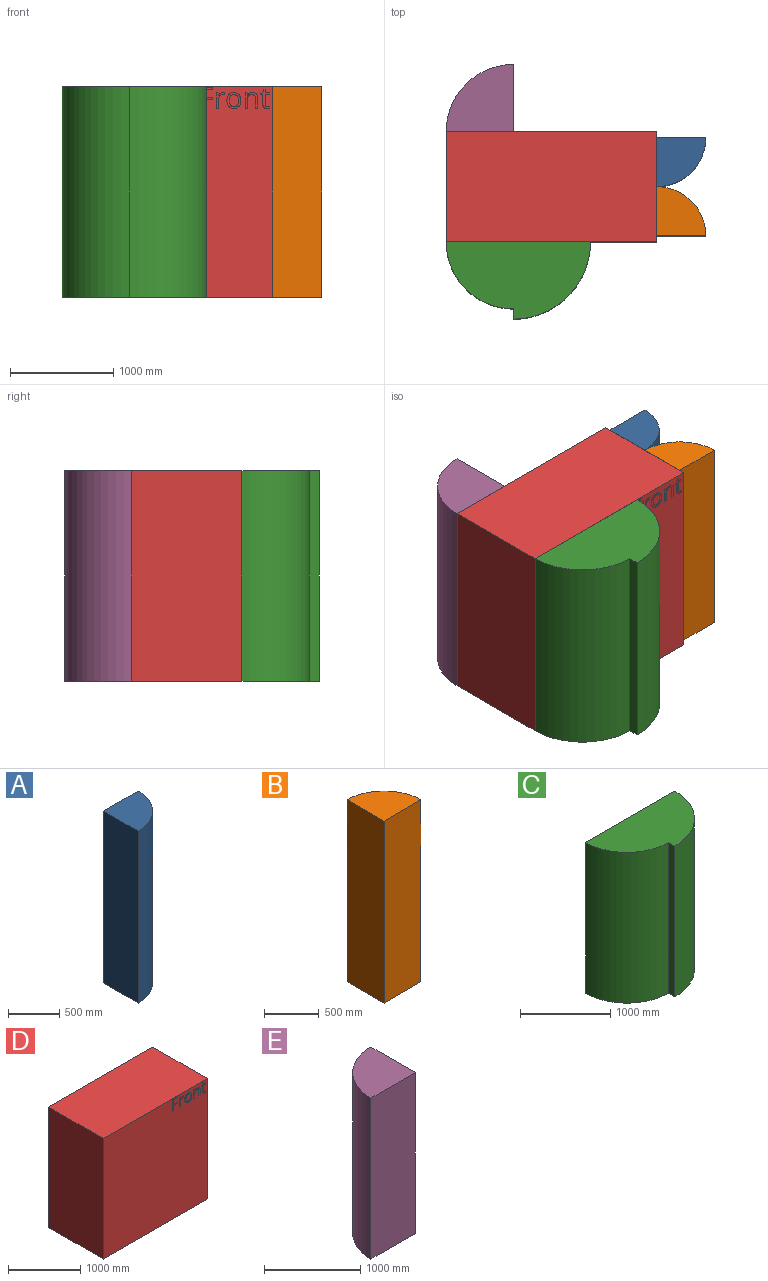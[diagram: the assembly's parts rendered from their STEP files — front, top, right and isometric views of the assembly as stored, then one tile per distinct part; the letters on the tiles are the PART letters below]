
ASSEMBLY  parts=5 mates=8
PART A: 5 faces, bbox 478x478x2045 mm
  f0: plane 2045x478mm, normal (-1,0,0), area 977510mm2, adj f1,f2,f3,f4
  f1: cylinder r=478mm len=2045mm, axis (0,0,-1), area 1535469.1mm2, adj f0,f2,f3,f4
  f2: plane 2045x478mm, normal (0,1,0), area 977510mm2, adj f0,f1,f3,f4
  f3: plane 478x478mm, normal (0,0,1), area 179450.9mm2, adj f0,f1,f2
  f4: plane 478x478mm, normal (0,0,-1), area 179450.9mm2, adj f0,f1,f2
PART B: 5 faces, bbox 478x478x2045 mm
  f0: cylinder r=478mm len=2045mm, axis (0,0,-1), area 1535469.1mm2, adj f1,f2,f3,f4
  f1: plane 2045x478mm, normal (-1,0,0), area 977510mm2, adj f0,f2,f3,f4
  f2: plane 2045x478mm, normal (0,-1,0), area 977510mm2, adj f0,f1,f3,f4
  f3: plane 478x478mm, normal (0,0,1), area 179450.9mm2, adj f0,f1,f2
  f4: plane 478x478mm, normal (0,0,-1), area 179450.9mm2, adj f0,f1,f2
PART C: 6 faces, bbox 1400x750x2045 mm
  f0: cylinder r=650mm len=2045mm, axis (0,0,-1), area 2087981mm2, adj f1,f3,f4,f5
  f1: plane 2045x100mm, normal (-1,0,0), area 204500mm2, adj f0,f2,f4,f5
  f2: cylinder r=750mm len=2045mm, axis (0,0,-1), area 2409208.9mm2, adj f1,f3,f4,f5
  f3: plane 2045x1400mm, normal (0,1,0), area 2863000mm2, adj f0,f2,f4,f5
  f4: plane 1400x750mm, normal (0,0,1), area 773617.2mm2, adj f0,f1,f2,f3
  f5: plane 1400x750mm, normal (0,0,-1), area 773617.2mm2, adj f0,f1,f2,f3
PART D: 88 faces, bbox 2040x1072x2045 mm
  f0: plane 2045x2040mm, normal (0,-1,0), area 4128266.2mm2, adj f2,f3,f4,f5,f6,f7,f8,f9
  f1: plane 2045x2040mm, normal (0,1,0), area 4171800mm2, adj f2,f3,f4,f5
  f2: plane 2045x1070mm, normal (-1,0,0), area 2188150mm2, adj f0,f1,f4,f5
  f3: plane 2045x1070mm, normal (1,0,0), area 2188150mm2, adj f0,f1,f4,f5
  f4: plane 2040x1070mm, normal (0,0,1), area 2182800mm2, adj f0,f1,f2,f3
  f5: plane 2040x1070mm, normal (0,0,-1), area 2182800mm2, adj f0,f1,f2,f3
  f6: plane 23.05x2mm, normal (0,0,-1), area 46.1mm2, adj f0,f7,f15,f16
  f7: plane 84.77x2mm, normal (1,0,0), area 169.5mm2, adj f0,f6,f8,f16
  f8: plane 82.21x2mm, normal (0,0,-1), area 164.4mm2, adj f0,f7,f9,f16
  f9: plane 20.49x2mm, normal (1,0,0), area 41mm2, adj f0,f8,f10,f16
  f10: plane 82.21x2mm, normal (0,0,1), area 164.4mm2, adj f0,f9,f11,f16
  f11: plane 72.57x2mm, normal (1,0,0), area 145.1mm2, adj f0,f10,f12,f16
  f12: plane 87.5x2mm, normal (0,0,-1), area 175mm2, adj f0,f11,f13,f16
  f13: plane 20.49x2mm, normal (1,0,0), area 41mm2, adj f0,f12,f14,f16
  f14: plane 110.55x2mm, normal (0,0,1), area 221.1mm2, adj f0,f13,f15,f16
  f15: plane 198.31x2mm, normal (-1,0,0), area 396.6mm2, adj f0,f6,f14,f16
  f16: plane 198.31x110.55mm, normal (0,-1,0), area 8047mm2, adj f6,f7,f8,f9,f10,f11,f12,f13
  f17: extruded ~17.75x2mm, area 35.7mm2, adj f0,f18,f29,f30
  f18: extruded ~25.65x7.88mm, area 54.5mm2, adj f0,f17,f19,f30
  f19: extruded ~22.37x19.92mm, area 60.5mm2, adj f0,f18,f20,f30
  f20: plane 2x1.09mm, normal (0,0,1), area 2.2mm2, adj f0,f19,f21,f30
  f21: plane 27.52x2.6mm, normal (1,0,0.09), area 55.3mm2, adj f0,f20,f22,f30
  f22: plane 18.58x2mm, normal (0,0,1), area 37.2mm2, adj f0,f21,f23,f30
  f23: plane 148.65x2mm, normal (-1,0,0), area 297.3mm2, adj f0,f22,f24,f30
  f24: plane 22.53x2mm, normal (0,0,-1), area 45.1mm2, adj f0,f23,f25,f30
  f25: plane 79.77x2mm, normal (1,0,0), area 159.5mm2, adj f0,f24,f26,f30
  f26: extruded ~36.48x12.8mm, area 79.1mm2, adj f0,f25,f27,f30
  f27: extruded ~30.86x14.65mm, area 70.6mm2, adj f0,f26,f28,f30
  f28: extruded ~16.28x2.04mm, area 32.9mm2, adj f0,f27,f29,f30
  f29: plane 20.88x3.13mm, normal (0.99,0,-0.15), area 42.2mm2, adj f0,f17,f28,f30
  f30: plane 151.39x85.59mm, normal (0,-1,0), area 4608.3mm2, adj f17,f18,f19,f20,f21,f22,f23,f24
  f31: extruded ~43.42x11.39mm, area 91.4mm2, adj f32,f47,f48,f49
  f32: extruded ~43.25x11.26mm, area 91mm2, adj f31,f33,f48,f49
  f33: extruded ~33.36x14.52mm, area 75.5mm2, adj f32,f34,f48,f49
  f34: extruded ~33.85x14.71mm, area 76.6mm2, adj f33,f35,f48,f49
  f35: extruded ~43.06x11.46mm, area 90.7mm2, adj f34,f36,f48,f49
  f36: extruded ~43.49x11.46mm, area 91.5mm2, adj f35,f37,f48,f49
  f37: extruded ~33.59x14.84mm, area 76.3mm2, adj f36,f47,f48,f49
  f38: extruded ~56.79x18.29mm, area 122.1mm2, adj f0,f39,f46,f48
  f39: extruded ~56.14x18.38mm, area 120.9mm2, adj f0,f38,f40,f48
  f40: extruded ~49.54x20.77mm, area 111mm2, adj f0,f39,f41,f48
  f41: extruded ~50.48x20.29mm, area 112.3mm2, adj f0,f40,f42,f48
  f42: extruded ~56.62x18.19mm, area 121.7mm2, adj f0,f41,f43,f48
  f43: extruded ~40.97x8.42mm, area 84.4mm2, adj f0,f42,f44,f48
  f44: extruded ~26.87x23.87mm, area 72.9mm2, adj f0,f43,f45,f48
  f45: extruded ~35.42x9.38mm, area 74.2mm2, adj f0,f44,f46,f48
  f46: extruded ~50.59x20.42mm, area 112.6mm2, adj f0,f38,f45,f48
  f47: extruded ~33.49x14.91mm, area 76.2mm2, adj f31,f37,f48,f49
  f48: plane 154.12x136.59mm, normal (0,-1,0), area 8488.3mm2, adj f31,f32,f33,f34,f35,f36,f37,f38
  f49: plane 116.1x89.93mm, normal (0,-1,0), area 8662.1mm2, adj f31,f32,f33,f34,f35,f36,f37,f47
  f50: plane 96.18x2mm, normal (-1,0,0), area 192.4mm2, adj f0,f51,f66,f67
  f51: plane 22.53x2mm, normal (0,0,-1), area 45.1mm2, adj f0,f50,f52,f67
  f52: plane 96.96x2mm, normal (1,0,0), area 193.9mm2, adj f0,f51,f53,f67
  f53: extruded ~41.47x13.56mm, area 89.7mm2, adj f0,f52,f54,f67
  f54: extruded ~40.43x12.96mm, area 87mm2, adj f0,f53,f55,f67
  f55: extruded ~27.8x6.05mm, area 57.4mm2, adj f0,f54,f56,f67
  f56: extruded ~19.42x17.04mm, area 52.4mm2, adj f0,f55,f57,f67
  f57: plane 2x1.09mm, normal (0,0,1), area 2.2mm2, adj f0,f56,f58,f67
  f58: plane 20.36x3.65mm, normal (0.98,0,0.18), area 41.4mm2, adj f0,f57,f59,f67
  f59: plane 18.32x2mm, normal (0,0,1), area 36.6mm2, adj f0,f58,f60,f67
  f60: plane 148.65x2mm, normal (-1,0,0), area 297.3mm2, adj f0,f59,f61,f67
  f61: plane 22.53x2mm, normal (0,0,-1), area 45.1mm2, adj f0,f60,f62,f67
  f62: plane 77.99x2mm, normal (1,0,0), area 156mm2, adj f0,f61,f63,f67
  f63: extruded ~41.65x10.85mm, area 87.8mm2, adj f0,f62,f64,f67
  f64: extruded ~34.16x12.61mm, area 75.2mm2, adj f0,f63,f65,f67
  f65: extruded ~25.93x8.96mm, area 56.5mm2, adj f0,f64,f66,f67
  f66: extruded ~27.11x8.27mm, area 58mm2, adj f0,f50,f65,f67
  f67: plane 151.39x124.26mm, normal (0,-1,0), area 8010.5mm2, adj f50,f51,f52,f53,f54,f55,f56,f57
  f68: extruded ~11.55x2mm, area 23.2mm2, adj f0,f69,f86,f87
  f69: extruded ~17.49x7.18mm, area 39mm2, adj f0,f68,f70,f87
  f70: extruded ~20.59x6.38mm, area 44.1mm2, adj f0,f69,f71,f87
  f71: plane 87.5x2mm, normal (1,0,0), area 175mm2, adj f0,f70,f72,f87
  f72: plane 43.14x2mm, normal (0,0,-1), area 86.3mm2, adj f0,f71,f73,f87
  f73: plane 17.49x2mm, normal (1,0,0), area 35mm2, adj f0,f72,f74,f87
  f74: plane 43.14x2mm, normal (0,0,1), area 86.3mm2, adj f0,f73,f75,f87
  f75: plane 34.46x2mm, normal (1,0,0), area 68.9mm2, adj f0,f74,f76,f87
  f76: plane 13.02x2mm, normal (0,0,1), area 26mm2, adj f0,f75,f77,f87
  f77: plane 31.73x9.46mm, normal (-0.96,0,0.29), area 66.2mm2, adj f0,f76,f78,f87
  f78: plane 21.31x9.38mm, normal (-0.4,0,0.92), area 46.6mm2, adj f0,f77,f79,f87
  f79: plane 10.85x2mm, normal (-1,0,0), area 21.7mm2, adj f0,f78,f80,f87
  f80: plane 21.31x2mm, normal (0,0,-1), area 42.6mm2, adj f0,f79,f81,f87
  f81: plane 88.46x2mm, normal (-1,0,0), area 176.9mm2, adj f0,f80,f82,f87
  f82: extruded ~45.44x43.1mm, area 143.7mm2, adj f0,f81,f83,f87
  f83: extruded ~12.85x2mm, area 25.8mm2, adj f0,f82,f84,f87
  f84: extruded ~10.76x2.91mm, area 22.4mm2, adj f0,f83,f85,f87
  f85: plane 17.23x2mm, normal (1,0,0), area 34.5mm2, adj f0,f84,f86,f87
  f86: extruded ~8.81x2mm, area 18mm2, adj f0,f68,f85,f87
  f87: plane 185.85x88.02mm, normal (0,-1,0), area 5717.6mm2, adj f68,f69,f70,f71,f72,f73,f74,f75
PART E: 5 faces, bbox 650x650x2045 mm
  f0: plane 2045x650mm, normal (0,-1,0), area 1329250mm2, adj f1,f2,f3,f4
  f1: plane 2045x650mm, normal (1,0,0), area 1329250mm2, adj f0,f2,f3,f4
  f2: cylinder r=650mm len=2045mm, axis (0,0,-1), area 2087981mm2, adj f0,f1,f3,f4
  f3: plane 650x650mm, normal (0,0,1), area 331830.7mm2, adj f0,f1,f2
  f4: plane 650x650mm, normal (0,0,-1), area 331830.7mm2, adj f0,f1,f2
PLACE A t=(1222.87,275.13,0)mm
PLACE B t=(1222.87,275.13,0)mm
PLACE C t=(1222.87,275.13,0)mm
PLACE D t=(1222.87,275.13,0)mm
PLACE E t=(1222.87,275.13,0)mm
MATE fastened B.f3 <-> D.f4  axis (0,0,1) through (2242.87,275.13,2045)mm
MATE planar B.f3 <-> D.f4  axis (0,0,1) through (2445.74,0,2045)mm
MATE fastened A.f3 <-> B.f3  axis (0,0,1) through (2242.87,275.13,2045)mm
MATE fastened C.f4 <-> D.f4  axis (0,0,1) through (202.87,-259.87,2045)mm
MATE planar E.f2 <-> D.f4  axis (0,0,1) through (852.87,810.13,2045)mm
MATE fastened E.f3 <-> D.f4  axis (0,0,1) through (202.87,810.13,2045)mm
MATE planar D.f4 <-> C.f4  axis (0,0,1) through (1222.87,275.13,2045)mm
MATE planar D.f4 <-> A.f3  axis (0,0,1) through (1222.87,275.13,2045)mm
